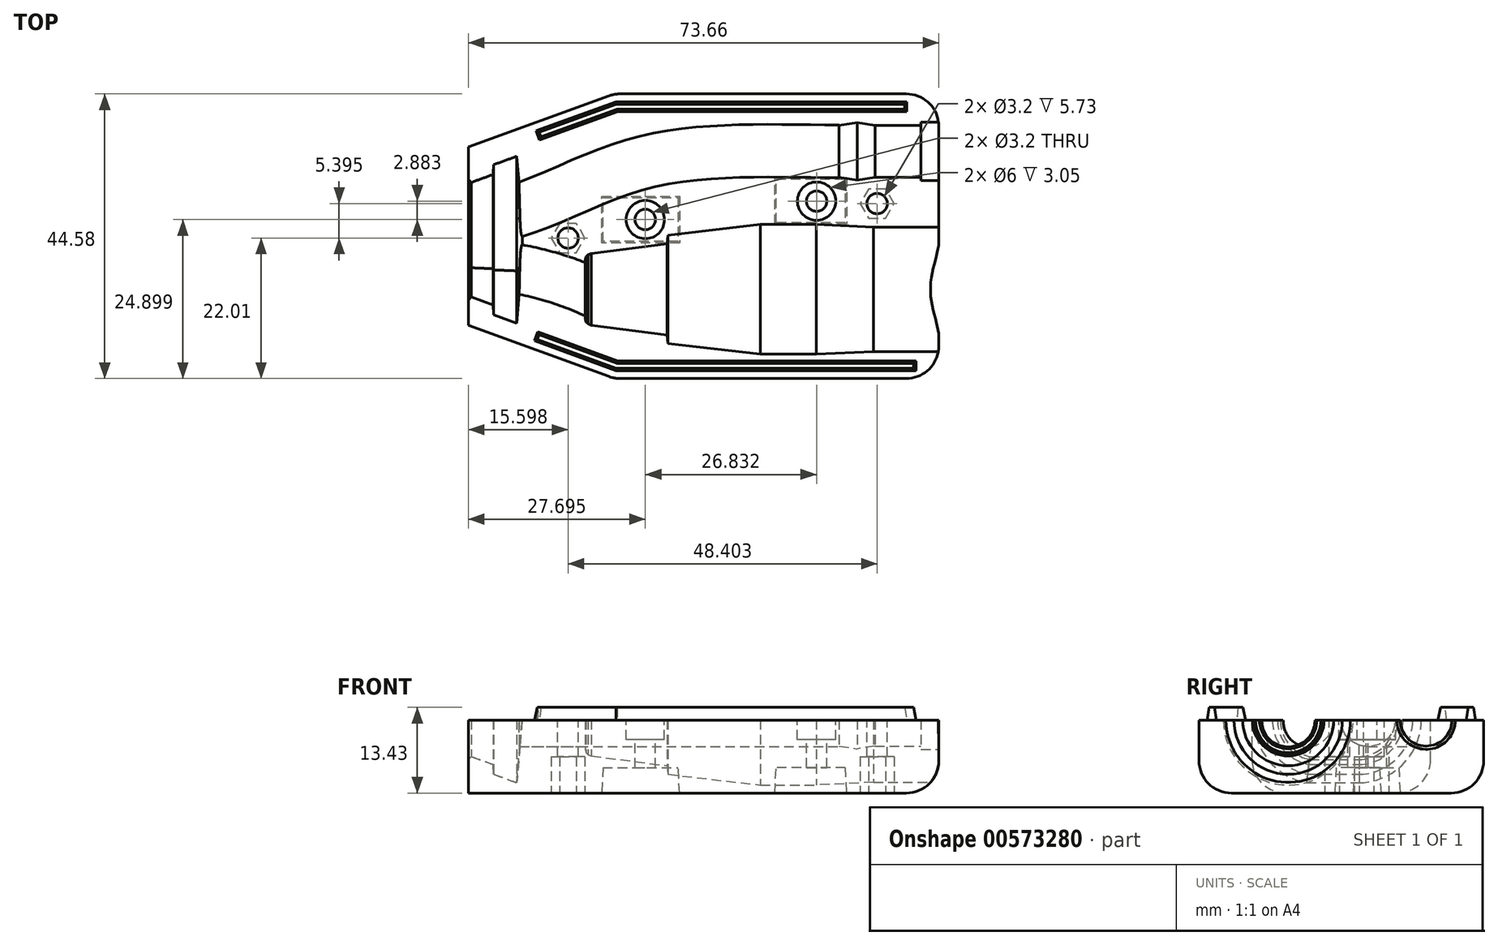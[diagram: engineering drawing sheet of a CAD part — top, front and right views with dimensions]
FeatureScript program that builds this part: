
annotation { "Feature Type Name" : "Feature", "Feature Type Description" : "" }
export const myFeature = defineFeature(function(context is Context, id is Id, definition is map)
    precondition{}
    {
        {
            var Q0;
            Q0=qCreatedBy(makeId("Top.planeOp"),FACE);
            var sketch = newSketch(context, id + "F0", { "sketchPlane" : qUnion([Q0])});
            skLineSegment(sketch, "E0", {"start": v(-29.16, 2.44) * mm, "end": v(45.25, 2.44) * mm});
            skLineSegment(sketch, "E1", {"start": v(45.25, 2.44) * mm, "end": v(45.25, -7.31) * mm});
            skLineSegment(sketch, "E2", {"start": v(45.25, -7.31) * mm, "end": v(33.01, -7.3) * mm});
            skLineSegment(sketch, "E3", {"start": v(33.01, -7.3) * mm, "end": v(31, -7.31) * mm});
            skLineSegment(sketch, "E4", {"start": v(31, -7.31) * mm, "end": v(16, -7.31) * mm});
            skLineSegment(sketch, "E5", {"start": v(16, -7.31) * mm, "end": v(7, -7.72) * mm});
            skLineSegment(sketch, "E6", {"start": v(7, -7.72) * mm, "end": v(-1.71, -7.72) * mm});
            skLineSegment(sketch, "E7", {"start": v(-1.71, -7.72) * mm, "end": v(-16.21, -6.04) * mm});
            skLineSegment(sketch, "E8", {"start": v(-16.21, -6.04) * mm, "end": v(-16.37, -4.7) * mm});
            skLineSegment(sketch, "E9", {"start": v(-16.37, -4.7) * mm, "end": v(-28.19, -3.17) * mm});
            skLineSegment(sketch, "E10", {"start": v(-28.19, -3.17) * mm, "end": v(-28.73, -2.96) * mm});
            skLineSegment(sketch, "E11", {"start": v(-28.73, -2.96) * mm, "end": v(-29.03, -2.68) * mm});
            skLineSegment(sketch, "E12", {"start": v(-29.03, -2.68) * mm, "end": v(-29.18, -2.06) * mm});
            skLineSegment(sketch, "E13", {"start": v(-29.18, -2.06) * mm, "end": v(-29.16, 2.44) * mm});
            skLineSegment(sketch, "E14.top", {"start": v(29.2, 18.83) * mm, "end": v(41.5, 18.83) * mm});
            skLineSegment(sketch, "E14.right", {"start": v(41.5, 24.03) * mm, "end": v(41.5, 18.83) * mm});
            skLineSegment(sketch, "E15", {"start": v(29.2, 19.46) * mm, "end": v(23.4, 19.46) * mm});
            skLineSegment(sketch, "E16", {"start": v(23.4, 19.46) * mm, "end": v(23.4, 24.03) * mm});
            skLineSegment(sketch, "E17", {"start": v(41.5, 24.03) * mm, "end": v(23.4, 24.03) * mm});
            skLineSegment(sketch, "E18", {"start": v(29.2, 18.83) * mm, "end": v(29.2, 19.46) * mm});
            skLineSegment(sketch, "E19.MirrorCS", {"start": v(-28.73, 7.85) * mm, "end": v(-29.03, 7.56) * mm});
            skLineSegment(sketch, "E20.MirrorCS", {"start": v(-29.03, 7.56) * mm, "end": v(-29.18, 6.94) * mm});
            skLineSegment(sketch, "E21.MirrorCS", {"start": v(33.01, 12.2) * mm, "end": v(31, 12.2) * mm});
            skLineSegment(sketch, "E22.MirrorCS", {"start": v(-28.19, 8.06) * mm, "end": v(-28.73, 7.85) * mm});
            skLineSegment(sketch, "E23.MirrorCS", {"start": v(-16.21, 10.93) * mm, "end": v(-16.37, 9.58) * mm});
            skLineSegment(sketch, "E24.MirrorCS", {"start": v(-16.37, 9.58) * mm, "end": v(-28.19, 8.06) * mm});
            skLineSegment(sketch, "E25.MirrorCS", {"start": v(7, 12.6) * mm, "end": v(-1.71, 12.6) * mm});
            skLineSegment(sketch, "E26.MirrorCS", {"start": v(45.25, 12.2) * mm, "end": v(33.01, 12.2) * mm});
            skLineSegment(sketch, "E27.MirrorCS", {"start": v(-1.71, 12.6) * mm, "end": v(-16.21, 10.93) * mm});
            skLineSegment(sketch, "E28.MirrorCS", {"start": v(16, 12.2) * mm, "end": v(7, 12.6) * mm});
            skLineSegment(sketch, "E29.MirrorCS", {"start": v(31, 12.2) * mm, "end": v(16, 12.2) * mm});
            skLineSegment(sketch, "E30.MirrorCS", {"start": v(45.25, 2.44) * mm, "end": v(45.25, 12.2) * mm});
            skLineSegment(sketch, "E31.MirrorCS", {"start": v(-29.18, 6.94) * mm, "end": v(-29.16, 2.44) * mm});
            skLineSegment(sketch, "E32", {"start": v(41.5, 20.03) * mm, "end": v(44.1, 20.03) * mm});
            skLineSegment(sketch, "E33", {"start": v(44.1, 20.03) * mm, "end": v(44.1, 24.03) * mm});
            skLineSegment(sketch, "E34", {"start": v(44.1, 24.03) * mm, "end": v(41.5, 24.03) * mm});
            skLineSegment(sketch, "E35", {"start": v(44.1, 20.03) * mm, "end": v(44.1, 19.46) * mm});
            skLineSegment(sketch, "E36", {"start": v(44.1, 19.46) * mm, "end": v(45.25, 19.46) * mm});
            skLineSegment(sketch, "E37", {"start": v(45.25, 19.46) * mm, "end": v(45.32, 24.03) * mm});
            skLineSegment(sketch, "E38", {"start": v(45.32, 24.03) * mm, "end": v(44.1, 24.03) * mm});
            skLineSegment(sketch, "E39", {"start": v(23.4, 24.03) * mm, "end": v(16.2, 24.03) * mm});
            skLineSegment(sketch, "E40", {"start": v(16.2, 24.03) * mm, "end": v(16.2, 19.98) * mm});
            skLineSegment(sketch, "E41", {"start": v(16.2, 19.98) * mm, "end": v(23.4, 19.98) * mm});
            skLineSegment(sketch, "E42", {"start": v(16.2, 19.98) * mm, "end": v(13.4, 19.53) * mm});
            skLineSegment(sketch, "E43", {"start": v(13.4, 19.53) * mm, "end": v(10.6, 19.98) * mm});
            skLineSegment(sketch, "E44", {"start": v(10.6, 19.98) * mm, "end": v(10.6, 24.03) * mm});
            skLineSegment(sketch, "E45", {"start": v(10.6, 24.03) * mm, "end": v(16.2, 24.03) * mm});
            skLineSegment(sketch, "E46.MirrorCS", {"start": v(44.1, 28.03) * mm, "end": v(44.1, 28.6) * mm});
            skLineSegment(sketch, "E47.MirrorCS", {"start": v(44.1, 28.6) * mm, "end": v(45.25, 28.6) * mm});
            skLineSegment(sketch, "E48.MirrorCS", {"start": v(29.2, 29.24) * mm, "end": v(29.2, 28.6) * mm});
            skLineSegment(sketch, "E49.MirrorCS", {"start": v(44.1, 28.03) * mm, "end": v(44.1, 24.03) * mm});
            skLineSegment(sketch, "E50.MirrorCS", {"start": v(16.2, 24.03) * mm, "end": v(16.2, 28.08) * mm});
            skLineSegment(sketch, "E51.MirrorCS", {"start": v(23.4, 28.6) * mm, "end": v(23.4, 24.03) * mm});
            skLineSegment(sketch, "E52.MirrorCS", {"start": v(10.6, 28.08) * mm, "end": v(10.6, 24.03) * mm});
            skLineSegment(sketch, "E53.MirrorCS", {"start": v(29.2, 28.6) * mm, "end": v(23.4, 28.6) * mm});
            skLineSegment(sketch, "E54.MirrorCS", {"start": v(41.5, 24.03) * mm, "end": v(41.5, 29.24) * mm});
            skLineSegment(sketch, "E55.MirrorCS", {"start": v(29.2, 29.24) * mm, "end": v(41.5, 29.24) * mm});
            skLineSegment(sketch, "E56.MirrorCS", {"start": v(45.25, 28.6) * mm, "end": v(45.32, 24.03) * mm});
            skLineSegment(sketch, "E57.MirrorCS", {"start": v(13.4, 28.53) * mm, "end": v(10.6, 28.08) * mm});
            skLineSegment(sketch, "E58.MirrorCS", {"start": v(41.5, 28.03) * mm, "end": v(44.1, 28.03) * mm});
            skLineSegment(sketch, "E59.MirrorCS", {"start": v(16.2, 28.08) * mm, "end": v(13.4, 28.53) * mm});
            skLineSegment(sketch, "E60.MirrorCS", {"start": v(16.2, 28.08) * mm, "end": v(23.4, 28.08) * mm});
            skSolve(sketch);
        }
        {
            var Q0;
            Q0=qCreatedBy(makeId("Top.planeOp"),FACE);
            var sketch = newSketch(context, id + "F1", { "sketchPlane" : qUnion([Q0])});
            skLineSegment(sketch, "E61.0", {"start": v(45.25, 2.44) * mm, "end": v(45.25, -7.31) * mm});
            skLineSegment(sketch, "E62", {"start": v(26.2, 33.05) * mm, "end": v(26.2, -11.53) * mm});
            skLineSegment(sketch, "E63", {"start": v(26.2, -11.53) * mm, "end": v(-24.6, -11.53) * mm});
            skLineSegment(sketch, "E64", {"start": v(-24.6, -11.53) * mm, "end": v(-47.46, -3.2) * mm});
            skLineSegment(sketch, "E65", {"start": v(-47.46, -3.2) * mm, "end": v(-47.46, 24.73) * mm});
            skLineSegment(sketch, "E66", {"start": v(-47.46, 24.73) * mm, "end": v(-24.6, 33.05) * mm});
            skLineSegment(sketch, "E67", {"start": v(-24.6, 33.05) * mm, "end": v(26.2, 33.05) * mm});
            skLineSegment(sketch, "E68.0", {"start": v(29.2, 29.24) * mm, "end": v(41.5, 29.24) * mm});
            skSolve(sketch);
        }
        {
            var Q0;
            Q0=qSketchRegion(id+"F1",true);
            extrude(context, id + "F2", {"entities" : qUnion([Q0]), "oppositeDirection" : true, "depth" : 11.43 * mm, "offsetDistance" : 25.4 * mm});
        }
        {
            var Q0;
            Q0=makeQuery(id+"F0.imprint","IMPRINT",FACE,{"disambiguationData":[TD([[makeQuery(id+"F0.imprint","IMPRINT",EDGE,{"derivedFrom":sQuery(id+"F0.wireOp",EDGE,"E0")}),-1.0]])]});
            var Q1;
            Q1=sQuery(id+"F0.wireOp",EDGE,"E0");
            revolve(context, id + "F3", {"operationType" : NewBodyOperationType.REMOVE, "entities" : qUnion([Q0]), "axis" : qUnion([Q1]), "revolveType" : RevolveType.FULL, "oppositeDirection" : true});
        }
        {
            var Q0;
            Q0=makeQuery(id+"F0.imprint","IMPRINT",FACE,{"disambiguationData":[TD([[makeQuery(id+"F0.imprint","IMPRINT",EDGE,{"derivedFrom":sQuery(id+"F0.wireOp",EDGE,"E14.top")}),1.0]])]});
            var Q1;
            Q1=makeQuery(id+"F0.imprint","IMPRINT",FACE,{"disambiguationData":[TD([[makeQuery(id+"F0.imprint","IMPRINT",EDGE,{"derivedFrom":sQuery(id+"F0.wireOp",EDGE,"E40")}),1.0]])]});
            var Q2;
            Q2=makeQuery(id+"F0.imprint","IMPRINT",FACE,{"disambiguationData":[TD([[makeQuery(id+"F0.imprint","IMPRINT",EDGE,{"derivedFrom":sQuery(id+"F0.wireOp",EDGE,"E40")}),-1.0]])]});
            var Q3;
            Q3=sQuery(id+"F0.wireOp",EDGE,"E17");
            revolve(context, id + "F4", {"operationType" : NewBodyOperationType.REMOVE, "entities" : qUnion([Q0, Q1, Q2]), "axis" : qUnion([Q3]), "revolveType" : RevolveType.FULL});
        }
        {
            var Q0;
            Q0=makeQuery(id+"F2.opExtrude","CAP_FACE",FACE,{"disambiguationData":[OSD([sQuery(id+"F1.wireOp",EDGE,"FN9DgEXL-DUnT-EqR8-ggIH-wTex11pTKOJ6"),sQuery(id+"F1.wireOp",EDGE,"Mmaicck8-LA38-ALDy-QV3c-pMFCgAv4KP83"),sQuery(id+"F1.wireOp",EDGE,"E62"),sQuery(id+"F1.wireOp",EDGE,"E63"),sQuery(id+"F1.wireOp",EDGE,"E64"),sQuery(id+"F1.wireOp",EDGE,"E65"),sQuery(id+"F1.wireOp",EDGE,"E66"),sQuery(id+"F1.wireOp",EDGE,"E67")])],"isStart":true});
            var sketch = newSketch(context, id + "F5", { "sketchPlane" : qUnion([Q0])});
            skLineSegment(sketch, "E69.0", {"start": v(-29.16, 2.44) * mm, "end": v(45.25, 2.44) * mm});
            skFitSpline(sketch, "E70", {"points": [v(-29.16, 2.44) * mm, v(-47.46, 6.7) * mm, v(-83.77, 9.93) * mm], "startDerivative": vector(-48.46, 20.5) * mm, "endDerivative": vector(-77.25, 2.74) * mm});
            skSolve(sketch);
        }
        {
            var Q0;
            Q0=sQuery(id+"F5.wireOp",VERTEX,"E70.0.internal");
            var Q1;
            Q1=sQuery(id+"F5.wireOp",EDGE,"E69.0");
            cPlane(context, id + "F6", {"entities" : qUnion([Q0, Q1]), "cplaneType" : CPlaneType.LINE_POINT, "offset" : 25.4 * mm, "width" : 152.4 * mm, "height" : 152.4 * mm});
        }
        {
            var Q0;
            Q0=qCreatedBy(id+"F6.planeOp",FACE);
            var sketch = newSketch(context, id + "F7", { "sketchPlane" : qUnion([Q0])});
            skCircle(sketch, "E71", {"center": v(2.44, 0) * mm, "radius": 4.2 * mm});
            skSolve(sketch);
        }
        {
            var Q0;
            Q0=qSketchRegion(id+"F7",true);
            var Q1;
            Q1=sQuery(id+"F5.wireOp",EDGE,"E70");
            sweep(context, id + "F8", {"operationType" : NewBodyOperationType.REMOVE, "profiles" : qUnion([Q0]), "path" : qUnion([Q1])});
        }
        {
            var Q0;
            Q0=sQuery(id+"F0.wireOp",VERTEX,"E45.start");
            var Q1;
            Q1=sQuery(id+"F0.wireOp",EDGE,"E45");
            cPlane(context, id + "F9", {"entities" : qUnion([Q0, Q1]), "cplaneType" : CPlaneType.LINE_POINT, "offset" : 25.4 * mm, "width" : 152.4 * mm, "height" : 152.4 * mm});
        }
        {
            var Q0;
            {var subQ0=sQuery(id+"F1.wireOp",EDGE,"E62");var subQ1=sQuery(id+"F1.wireOp",EDGE,"E65");var subQ2=sQuery(id+"F1.wireOp",EDGE,"E66");var subQ3=sQuery(id+"F1.wireOp",EDGE,"E67");Q0=makeQuery(id+"F8.boolean.opBoolean","SPLIT",FACE,{"disambiguationData":[TD([makeQuery(id+"F2.opExtrude","SWEPT_FACE",FACE,{"disambiguationData":[OSD([subQ2])]})])],"derivedFrom":makeQuery(id+"F2.opExtrude","CAP_FACE",FACE,{"disambiguationData":[OSD([subQ0,sQuery(id+"F1.wireOp",EDGE,"E63"),sQuery(id+"F1.wireOp",EDGE,"E64"),subQ1,subQ2,subQ3])],"isStart":true})});}
            var sketch = newSketch(context, id + "F10", { "sketchPlane" : qUnion([Q0])});
            skLineSegment(sketch, "E72.0", {"start": v(10.6, 24.03) * mm, "end": v(16.2, 24.03) * mm});
            skFitSpline(sketch, "E73", {"points": [v(10.6, 24.03) * mm, v(-17.54, 22.88) * mm, v(-35.92, 16.19) * mm, v(-61.27, 13.83) * mm], "startDerivative": vector(-66.57, 0.28) * mm, "endDerivative": vector(-121.3, 10.88) * mm});
            skSolve(sketch);
        }
        {
            var Q0;
            Q0=qCreatedBy(id+"F9.planeOp",FACE);
            var sketch = newSketch(context, id + "F11", { "sketchPlane" : qUnion([Q0])});
            skCircle(sketch, "E74", {"center": v(24.03, 0) * mm, "radius": 4.12 * mm});
            skSolve(sketch);
        }
        {
            var Q0;
            Q0=qSketchRegion(id+"F11",true);
            var Q1;
            Q1=sQuery(id+"F10.wireOp",EDGE,"E73");
            sweep(context, id + "F12", {"operationType" : NewBodyOperationType.REMOVE, "profiles" : qUnion([Q0]), "path" : qUnion([Q1])});
        }
        {
            var Q0;
            {var subQ4=sQuery(id+"F1.wireOp",EDGE,"E62");var subQ8=makeQuery(id+"F3.boolean.opBoolean","COPY",FACE,{"derivedFrom":makeQuery(id+"F3.opRevolve","SWEPT_FACE",FACE,{"disambiguationData":[OSD([sQuery(id+"F0.wireOp",EDGE,"E4")])]})});var subQ15=sQuery(id+"F1.wireOp",EDGE,"E65");var subQ16=sQuery(id+"F1.wireOp",EDGE,"E66");var subQ17=sQuery(id+"F1.wireOp",EDGE,"E67");Q0=makeQuery(id+"F12.boolean.opBoolean","SPLIT",FACE,{"disambiguationData":[TD([subQ8])],"derivedFrom":makeQuery(id+"F8.boolean.opBoolean","SPLIT",FACE,{"disambiguationData":[TD([makeQuery(id+"F2.opExtrude","SWEPT_FACE",FACE,{"disambiguationData":[OSD([subQ16])]})])],"derivedFrom":makeQuery(id+"F2.opExtrude","CAP_FACE",FACE,{"disambiguationData":[OSD([subQ4,sQuery(id+"F1.wireOp",EDGE,"E63"),sQuery(id+"F1.wireOp",EDGE,"E64"),subQ15,subQ16,subQ17])],"isStart":true})})});}
            var sketch = newSketch(context, id + "F13", { "sketchPlane" : qUnion([Q0])});
            skCircle(sketch, "E75", {"center": v(7.07, 16.25) * mm, "radius": 3 * mm});
            skCircle(sketch, "E76", {"center": v(-19.76, 13.37) * mm, "radius": 3 * mm});
            skSolve(sketch);
        }
        {
            var Q0;
            Q0=qSketchRegion(id+"F13",true);
            extrude(context, id + "F14", {"entities" : qUnion([Q0]), "operationType" : NewBodyOperationType.REMOVE, "oppositeDirection" : true, "depth" : 3.05 * mm, "offsetDistance" : 25.4 * mm});
        }
        {
            var Q0;
            {var subQ4=sQuery(id+"F1.wireOp",EDGE,"E62");var subQ7=sQuery(id+"F1.wireOp",EDGE,"E65");var subQ8=makeQuery(id+"F2.opExtrude","SWEPT_FACE",FACE,{"disambiguationData":[OSD([subQ7])]});var subQ10=sQuery(id+"F1.wireOp",EDGE,"E66");var subQ11=makeQuery(id+"F2.opExtrude","SWEPT_FACE",FACE,{"disambiguationData":[OSD([subQ10])]});var subQ12=sQuery(id+"F1.wireOp",EDGE,"E67");Q0=makeQuery(id+"F12.boolean.opBoolean","SPLIT",FACE,{"disambiguationData":[TD([subQ8])],"derivedFrom":makeQuery(id+"F8.boolean.opBoolean","SPLIT",FACE,{"disambiguationData":[TD([subQ11])],"derivedFrom":makeQuery(id+"F2.opExtrude","CAP_FACE",FACE,{"disambiguationData":[OSD([subQ4,sQuery(id+"F1.wireOp",EDGE,"E63"),sQuery(id+"F1.wireOp",EDGE,"E64"),subQ7,subQ10,subQ12])],"isStart":true})})});}
            var sketch = newSketch(context, id + "F15", { "sketchPlane" : qUnion([Q0])});
            skLineSegment(sketch, "E77.0", {"start": v(-24.38, 31.8) * mm, "end": v(21.2, 31.8) * mm});
            skLineSegment(sketch, "E77.1", {"start": v(-36.84, 27.26) * mm, "end": v(-24.38, 31.8) * mm});
            skPoint(sketch, "E78", {"position": v(21.2, 31.8) * mm});
            skPoint(sketch, "E79", {"position": v(-36.84, 27.26) * mm});
            skLineSegment(sketch, "E80.0", {"start": v(-24.11, 30.3) * mm, "end": v(21.2, 30.3) * mm});
            skLineSegment(sketch, "E80.1", {"start": v(-36.33, 25.85) * mm, "end": v(-24.11, 30.3) * mm});
            skLineSegment(sketch, "E81", {"start": v(21.2, 30.3) * mm, "end": v(21.2, 31.8) * mm});
            skLineSegment(sketch, "E82", {"start": v(-36.84, 27.26) * mm, "end": v(-36.33, 25.85) * mm});
            skLineSegment(sketch, "E83.0", {"start": v(-24.38, -10.28) * mm, "end": v(-37.13, -5.64) * mm});
            skLineSegment(sketch, "E83.1", {"start": v(22.64, -10.28) * mm, "end": v(-24.38, -10.28) * mm});
            skPoint(sketch, "E84", {"position": v(22.64, -10.28) * mm});
            skPoint(sketch, "E85", {"position": v(-37.13, -5.64) * mm});
            skLineSegment(sketch, "E86.0", {"start": v(-24.11, -8.78) * mm, "end": v(-36.62, -4.23) * mm});
            skLineSegment(sketch, "E86.1", {"start": v(22.64, -8.78) * mm, "end": v(-24.11, -8.78) * mm});
            skLineSegment(sketch, "E87", {"start": v(22.64, -10.28) * mm, "end": v(22.64, -8.78) * mm});
            skLineSegment(sketch, "E88", {"start": v(-37.13, -5.64) * mm, "end": v(-36.62, -4.23) * mm});
            skSolve(sketch);
        }
        {
            var Q0;
            {var subQ4=sQuery(id+"F1.wireOp",EDGE,"E62");var subQ8=makeQuery(id+"F3.boolean.opBoolean","COPY",FACE,{"derivedFrom":makeQuery(id+"F3.opRevolve","SWEPT_FACE",FACE,{"disambiguationData":[OSD([sQuery(id+"F0.wireOp",EDGE,"E4")])]})});var subQ19=sQuery(id+"F1.wireOp",EDGE,"E65");var subQ20=sQuery(id+"F1.wireOp",EDGE,"E66");var subQ21=sQuery(id+"F1.wireOp",EDGE,"E67");Q0=makeQuery(id+"F12.boolean.opBoolean","SPLIT",FACE,{"disambiguationData":[TD([subQ8])],"derivedFrom":makeQuery(id+"F8.boolean.opBoolean","SPLIT",FACE,{"disambiguationData":[TD([makeQuery(id+"F2.opExtrude","SWEPT_FACE",FACE,{"disambiguationData":[OSD([subQ20])]})])],"derivedFrom":makeQuery(id+"F2.opExtrude","CAP_FACE",FACE,{"disambiguationData":[OSD([subQ4,sQuery(id+"F1.wireOp",EDGE,"E63"),sQuery(id+"F1.wireOp",EDGE,"E64"),subQ19,subQ20,subQ21])],"isStart":true})})});}
            var sketch = newSketch(context, id + "F16", { "sketchPlane" : qUnion([Q0])});
            skCircle(sketch, "E89", {"center": v(-19.76, 13.37) * mm, "radius": 1.6 * mm});
            skCircle(sketch, "E90", {"center": v(7.07, 16.25) * mm, "radius": 1.6 * mm});
            skSolve(sketch);
        }
        {
            var Q0;
            Q0=makeQuery(id+"F16.imprint","IMPRINT",FACE,{"disambiguationData":[TD([[makeQuery(id+"F16.imprint","IMPRINT",EDGE,{"derivedFrom":sQuery(id+"F16.wireOp",EDGE,"E89")}),1.0]])]});
            var Q1;
            Q1=makeQuery(id+"F16.imprint","IMPRINT",FACE,{"disambiguationData":[TD([[makeQuery(id+"F16.imprint","IMPRINT",EDGE,{"derivedFrom":sQuery(id+"F16.wireOp",EDGE,"E90")}),1.0]])]});
            extrude(context, id + "F17", {"entities" : qUnion([Q0, Q1]), "operationType" : NewBodyOperationType.REMOVE, "oppositeDirection" : true, "depth" : 25.4 * mm, "offsetDistance" : 25.4 * mm});
        }
        {
            var Q0;
            Q0=qSketchRegion(id+"F15",true);
            extrude(context, id + "F18", {"entities" : qUnion([Q0]), "operationType" : NewBodyOperationType.ADD, "depth" : 2 * mm, "offsetDistance" : 25.4 * mm, "hasDraft" : true, "draftAngle" : 10 * degree, "draftPullDirection" : true});
        }
        {
            var Q0;
            Q0=makeQuery(id+"F2.opExtrude","CAP_FACE",FACE,{"disambiguationData":[OSD([sQuery(id+"F1.wireOp",EDGE,"E62"),sQuery(id+"F1.wireOp",EDGE,"E63"),sQuery(id+"F1.wireOp",EDGE,"E64"),sQuery(id+"F1.wireOp",EDGE,"E65"),sQuery(id+"F1.wireOp",EDGE,"E66"),sQuery(id+"F1.wireOp",EDGE,"E67")])],"isStart":false});
            var sketch = newSketch(context, id + "F19", { "sketchPlane" : qUnion([Q0])});
            skLineSegment(sketch, "E91.bottom", {"start": v(0.52, -12.67) * mm, "end": v(11.75, -12.67) * mm});
            skLineSegment(sketch, "E91.top", {"start": v(0.52, -19.97) * mm, "end": v(11.75, -19.97) * mm});
            skLineSegment(sketch, "E91.left", {"start": v(0.52, -12.67) * mm, "end": v(0.52, -19.97) * mm});
            skLineSegment(sketch, "E91.right", {"start": v(11.75, -12.67) * mm, "end": v(11.75, -19.97) * mm});
            skLineSegment(sketch, "E92.bottom", {"start": v(-14.4, -17.02) * mm, "end": v(-26.6, -17.02) * mm});
            skLineSegment(sketch, "E92.top", {"start": v(-14.4, -9.72) * mm, "end": v(-26.6, -9.72) * mm});
            skLineSegment(sketch, "E92.left", {"start": v(-14.4, -17.02) * mm, "end": v(-14.4, -9.72) * mm});
            skLineSegment(sketch, "E92.right", {"start": v(-26.6, -17.02) * mm, "end": v(-26.6, -9.72) * mm});
            skSolve(sketch);
        }
        {
            var Q0;
            Q0=qSketchRegion(id+"F19",true);
            extrude(context, id + "F20", {"entities" : qUnion([Q0]), "operationType" : NewBodyOperationType.REMOVE, "oppositeDirection" : true, "depth" : 4 * mm, "offsetDistance" : 25.4 * mm, "hasDraft" : true, "draftAngle" : 3 * degree, "draftPullDirection" : true});
        }
        {
            var Q0;
            Q0=makeQuery(id+"F2.opExtrude","SWEPT_EDGE",EDGE,{"disambiguationData":[OSD([sQuery(id+"F1.wireOp",EDGE,"E62"),sQuery(id+"F1.wireOp",EDGE,"E63")])]});
            var Q1;
            Q1=makeQuery(id+"F2.opExtrude","CAP_EDGE",EDGE,{"disambiguationData":[OSD([sQuery(id+"F1.wireOp",EDGE,"E63")])],"isStart":false});
            var Q2;
            Q2=makeQuery(id+"F2.opExtrude","CAP_EDGE",EDGE,{"disambiguationData":[OSD([sQuery(id+"F1.wireOp",EDGE,"E62")])],"isStart":false});
            var Q3;
            Q3=makeQuery(id+"F2.opExtrude","CAP_EDGE",EDGE,{"disambiguationData":[OSD([sQuery(id+"F1.wireOp",EDGE,"E64")])],"isStart":false});
            var Q4;
            Q4=makeQuery(id+"F2.opExtrude","SWEPT_EDGE",EDGE,{"disambiguationData":[OSD([sQuery(id+"F1.wireOp",EDGE,"E63"),sQuery(id+"F1.wireOp",EDGE,"E64")])]});
            var Q5;
            Q5=makeQuery(id+"F2.opExtrude","CAP_EDGE",EDGE,{"disambiguationData":[OSD([sQuery(id+"F1.wireOp",EDGE,"E66")])],"isStart":false});
            var Q6;
            Q6=makeQuery(id+"F2.opExtrude","SWEPT_EDGE",EDGE,{"disambiguationData":[OSD([sQuery(id+"F1.wireOp",EDGE,"E66"),sQuery(id+"F1.wireOp",EDGE,"E67")])]});
            var Q7;
            Q7=makeQuery(id+"F2.opExtrude","CAP_EDGE",EDGE,{"disambiguationData":[OSD([sQuery(id+"F1.wireOp",EDGE,"E67")])],"isStart":false});
            var Q8;
            Q8=makeQuery(id+"F2.opExtrude","SWEPT_EDGE",EDGE,{"disambiguationData":[OSD([sQuery(id+"F1.wireOp",EDGE,"E62"),sQuery(id+"F1.wireOp",EDGE,"E67")])]});
            fillet(context, id + "F21", {"entities" : qUnion([Q0, Q1, Q2, Q3, Q4, Q5, Q6, Q7, Q8]), "radius" : 5.08 * mm, "tangentPropagation" : true, "allowEdgeOverflow" : false});
        }
        {
            var Q0;
            {var subQ4=sQuery(id+"F1.wireOp",EDGE,"E62");var subQ8=makeQuery(id+"F3.boolean.opBoolean","COPY",FACE,{"derivedFrom":makeQuery(id+"F3.opRevolve","SWEPT_FACE",FACE,{"disambiguationData":[OSD([sQuery(id+"F0.wireOp",EDGE,"E4")])]})});var subQ19=sQuery(id+"F1.wireOp",EDGE,"E65");var subQ20=sQuery(id+"F1.wireOp",EDGE,"E66");var subQ21=sQuery(id+"F1.wireOp",EDGE,"E67");Q0=makeQuery(id+"F12.boolean.opBoolean","SPLIT",FACE,{"disambiguationData":[TD([subQ8])],"derivedFrom":makeQuery(id+"F8.boolean.opBoolean","SPLIT",FACE,{"disambiguationData":[TD([makeQuery(id+"F2.opExtrude","SWEPT_FACE",FACE,{"disambiguationData":[OSD([subQ20])]})])],"derivedFrom":makeQuery(id+"F2.opExtrude","CAP_FACE",FACE,{"disambiguationData":[OSD([subQ4,sQuery(id+"F1.wireOp",EDGE,"E63"),sQuery(id+"F1.wireOp",EDGE,"E64"),subQ19,subQ20,subQ21])],"isStart":true})})});}
            var sketch = newSketch(context, id + "F22", { "sketchPlane" : qUnion([Q0])});
            skCircle(sketch, "E93", {"center": v(-31.86, 10.48) * mm, "radius": 1.6 * mm});
            skCircle(sketch, "E94", {"center": v(16.54, 15.88) * mm, "radius": 1.6 * mm});
            skSolve(sketch);
        }
        {
            var Q0;
            Q0=qSketchRegion(id+"F22",true);
            extrude(context, id + "F23", {"entities" : qUnion([Q0]), "operationType" : NewBodyOperationType.REMOVE, "oppositeDirection" : true, "depth" : 25.4 * mm, "offsetDistance" : 25.4 * mm});
        }
        {
            var Q0;
            Q0=makeQuery(id+"F2.opExtrude","CAP_FACE",FACE,{"disambiguationData":[OSD([sQuery(id+"F1.wireOp",EDGE,"E62"),sQuery(id+"F1.wireOp",EDGE,"E63"),sQuery(id+"F1.wireOp",EDGE,"E64"),sQuery(id+"F1.wireOp",EDGE,"E65"),sQuery(id+"F1.wireOp",EDGE,"E66"),sQuery(id+"F1.wireOp",EDGE,"E67")])],"isStart":false});
            var sketch = newSketch(context, id + "F24", { "sketchPlane" : qUnion([Q0])});
            skCircle(sketch, "E95.0", {"center": v(-31.86, -10.48) * mm, "radius": 1.6 * mm});
            skCircle(sketch, "E96.0", {"center": v(16.54, -15.88) * mm, "radius": 1.6 * mm});
            skCircle(sketch, "E97.cCircle", {"center": v(-31.86, -10.48) * mm, "radius": 2.65 * mm, "construction": true});
            skLineSegment(sketch, "E97.0", {"start": v(-29.21, -10.48) * mm, "end": v(-30.54, -12.78) * mm});
            skLineSegment(sketch, "E97.1", {"start": v(-30.54, -12.78) * mm, "end": v(-33.19, -12.78) * mm});
            skLineSegment(sketch, "E97.2", {"start": v(-33.19, -12.78) * mm, "end": v(-34.51, -10.48) * mm});
            skLineSegment(sketch, "E97.3", {"start": v(-34.51, -10.48) * mm, "end": v(-33.19, -8.19) * mm});
            skLineSegment(sketch, "E97.4", {"start": v(-33.19, -8.19) * mm, "end": v(-30.54, -8.19) * mm});
            skLineSegment(sketch, "E97.5", {"start": v(-30.54, -8.19) * mm, "end": v(-29.21, -10.48) * mm});
            skCircle(sketch, "E98.cCircle", {"center": v(16.54, -15.88) * mm, "radius": 2.65 * mm, "construction": true});
            skLineSegment(sketch, "E98.0", {"start": v(19.2, -15.88) * mm, "end": v(17.87, -18.17) * mm});
            skLineSegment(sketch, "E98.1", {"start": v(17.87, -18.17) * mm, "end": v(15.22, -18.17) * mm});
            skLineSegment(sketch, "E98.2", {"start": v(15.22, -18.17) * mm, "end": v(13.9, -15.88) * mm});
            skLineSegment(sketch, "E98.3", {"start": v(13.9, -15.88) * mm, "end": v(15.22, -13.58) * mm});
            skLineSegment(sketch, "E98.4", {"start": v(15.22, -13.58) * mm, "end": v(17.87, -13.58) * mm});
            skLineSegment(sketch, "E98.5", {"start": v(17.87, -13.58) * mm, "end": v(19.2, -15.88) * mm});
            skSolve(sketch);
        }
        {
            var Q0;
            Q0=qSketchRegion(id+"F24",true);
            extrude(context, id + "F25", {"entities" : qUnion([Q0]), "operationType" : NewBodyOperationType.REMOVE, "oppositeDirection" : true, "depth" : 5.7 * mm, "offsetDistance" : 25.4 * mm});
        }
        {
            var Q0;
            Q0=makeQuery(id+"F2.opExtrude","SWEPT_FACE",FACE,{"disambiguationData":[OSD([sQuery(id+"F1.wireOp",EDGE,"E65")])]});
            var sketch = newSketch(context, id + "F26", { "sketchPlane" : qUnion([Q0])});
            skArc(sketch, "E99", {"start": v(-17.6, 0) * mm, "mid": v(-16.4, -2.9) * mm, "end": v(-13.51, -4.12) * mm});
            skArc(sketch, "E100", {"start": v(-6, -4.12) * mm, "mid": v(-3.69, -2.62) * mm, "end": v(-2.8, 0) * mm});
            skLineSegment(sketch, "E101", {"start": v(-13.51, -4.12) * mm, "end": v(-6, -4.12) * mm});
            skSolve(sketch);
        }
        {
            var Q0;
            {var subQ4=sQuery(id+"F1.wireOp",EDGE,"E62");var subQ8=makeQuery(id+"F3.boolean.opBoolean","COPY",FACE,{"derivedFrom":makeQuery(id+"F3.opRevolve","SWEPT_FACE",FACE,{"disambiguationData":[OSD([sQuery(id+"F0.wireOp",EDGE,"E4")])]})});var subQ19=sQuery(id+"F1.wireOp",EDGE,"E65");var subQ20=sQuery(id+"F1.wireOp",EDGE,"E66");var subQ21=sQuery(id+"F1.wireOp",EDGE,"E67");Q0=makeQuery(id+"F12.boolean.opBoolean","SPLIT",FACE,{"disambiguationData":[TD([subQ8])],"derivedFrom":makeQuery(id+"F8.boolean.opBoolean","SPLIT",FACE,{"disambiguationData":[TD([makeQuery(id+"F2.opExtrude","SWEPT_FACE",FACE,{"disambiguationData":[OSD([subQ20])]})])],"derivedFrom":makeQuery(id+"F2.opExtrude","CAP_FACE",FACE,{"disambiguationData":[OSD([subQ4,sQuery(id+"F1.wireOp",EDGE,"E63"),sQuery(id+"F1.wireOp",EDGE,"E64"),subQ19,subQ20,subQ21])],"isStart":true})})});}
            var sketch = newSketch(context, id + "F27", { "sketchPlane" : qUnion([Q0])});
            skLineSegment(sketch, "E102", {"start": v(-39.23, 4.74) * mm, "end": v(-39.9, -2.86) * mm});
            skLineSegment(sketch, "E103", {"start": v(-43.55, -1.54) * mm, "end": v(-43.57, -0.02) * mm});
            skLineSegment(sketch, "E104", {"start": v(-47, 1.23) * mm, "end": v(-49.56, -1.34) * mm});
            skLineSegment(sketch, "E105", {"start": v(-49.56, -1.34) * mm, "end": v(-50.55, 5.78) * mm});
            skLineSegment(sketch, "E106", {"start": v(-50.55, 5.78) * mm, "end": v(-39.23, 4.74) * mm});
            skLineSegment(sketch, "E107", {"start": v(-47, 1.23) * mm, "end": v(-43.57, -0.02) * mm});
            skLineSegment(sketch, "E108", {"start": v(-43.55, -1.54) * mm, "end": v(-39.9, -2.86) * mm});
            skSolve(sketch);
        }
        {
            var Q0;
            Q0=makeQuery(id+"F27.imprint","IMPRINT",FACE,{"disambiguationData":[TD([[makeQuery(id+"F27.imprint","IMPRINT",EDGE,{"derivedFrom":sQuery(id+"F27.wireOp",EDGE,"E102")}),-1.0]])]});
            var Q1;
            Q1=sQuery(id+"F26.wireOp",EDGE,"E101");
            var Q2;
            Q2=sQuery(id+"F26.wireOp",EDGE,"E100");
            var Q3;
            Q3=sQuery(id+"F26.wireOp",EDGE,"E99");
            sweep(context, id + "F28", {"operationType" : NewBodyOperationType.REMOVE, "profiles" : qUnion([Q0]), "path" : qUnion([Q1, Q2, Q3])});
        }
        {
            var Q0;
            Q0=makeQuery(id+"F28.boolean.opBoolean","COPY",FACE,{"derivedFrom":makeQuery(id+"F28.opSweep","SWEPT_FACE",FACE,{"disambiguationData":[OSD([sQuery(id+"F26.wireOp",EDGE,"E101"),sQuery(id+"F27.wireOp",EDGE,"E102")])]})});
            var sketch = newSketch(context, id + "F29", { "sketchPlane" : qUnion([Q0])});
            skLineSegment(sketch, "E109", {"start": v(-6, -7.61) * mm, "end": v(-13.5, -7.34) * mm});
            skLineSegment(sketch, "E110", {"start": v(-13.5, -7.34) * mm, "end": v(-16.02, 2.25) * mm});
            skLineSegment(sketch, "E111", {"start": v(-16.02, 2.25) * mm, "end": v(-3.6, 1.18) * mm});
            skLineSegment(sketch, "E112", {"start": v(-3.6, 1.18) * mm, "end": v(-6, -7.61) * mm});
            skSolve(sketch);
        }
        {
            var Q0;
            Q0 = qSketchRegion(id + "F29", true);
            extrude(context, id + "F30", {"entities" : qUnion([Q0]), "operationType" : NewBodyOperationType.REMOVE, "depth" : 25.4 * mm, "offsetDistance" : 25.4 * mm});
        }
    });
